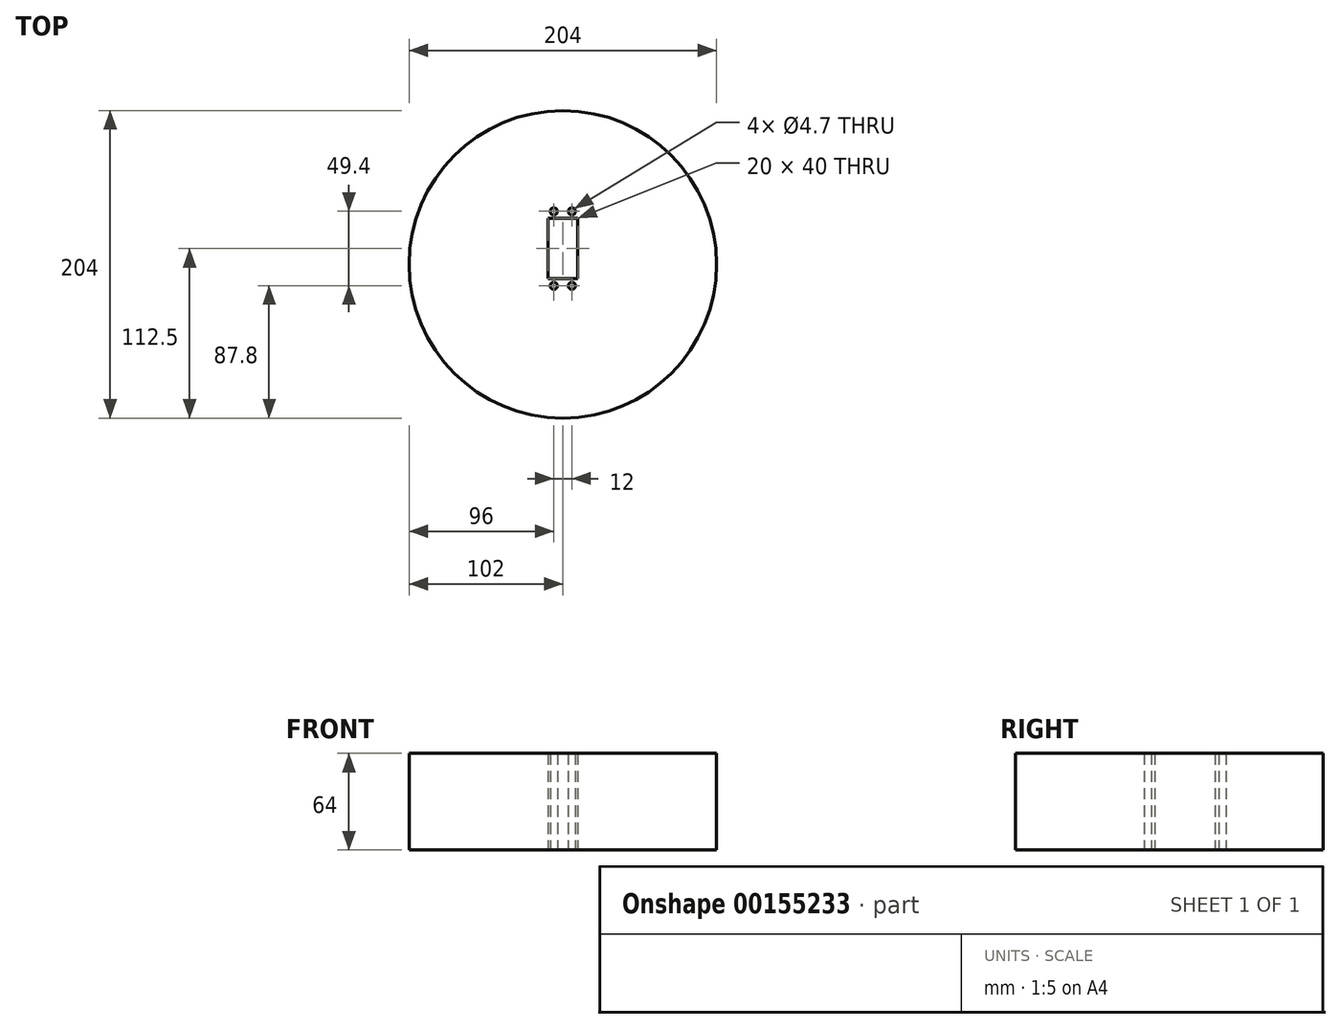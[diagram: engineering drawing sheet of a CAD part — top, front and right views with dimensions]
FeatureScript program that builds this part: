
annotation { "Feature Type Name" : "Feature", "Feature Type Description" : "" }
export const myFeature = defineFeature(function(context is Context, id is Id, definition is map)
    precondition{}
    {
        {
            var Q0;
            Q0=qCreatedBy(makeId("Top.planeOp"),FACE);
            var sketch = newSketch(context, id + "F0", { "sketchPlane" : qUnion([Q0])});
            skLineSegment(sketch, "E0.bottom", {"start": v(-10, -9.5) * mm, "end": v(10, -9.5) * mm});
            skLineSegment(sketch, "E0.top", {"start": v(-10, 30.5) * mm, "end": v(10, 30.5) * mm});
            skLineSegment(sketch, "E0.left", {"start": v(-10, -9.5) * mm, "end": v(-10, 30.5) * mm});
            skLineSegment(sketch, "E0.right", {"start": v(10, -9.5) * mm, "end": v(10, 30.5) * mm});
            skCircle(sketch, "E1", {"center": v(0, 0) * mm, "radius": 102 * mm});
            skCircle(sketch, "E2", {"center": v(-6, 35.2) * mm, "radius": 2.35 * mm});
            skCircle(sketch, "E3", {"center": v(6, 35.2) * mm, "radius": 2.35 * mm});
            skCircle(sketch, "E4", {"center": v(-6, -14.2) * mm, "radius": 2.35 * mm});
            skCircle(sketch, "E5", {"center": v(6, -14.2) * mm, "radius": 2.35 * mm});
            skSolve(sketch);
        }
        {
            var Q0;
            Q0 = qSketchRegion(id + "F0", true);
            extrude(context, id + "F1", {"entities" : qUnion([Q0]), "depth" : 64 * mm});
        }
    });
